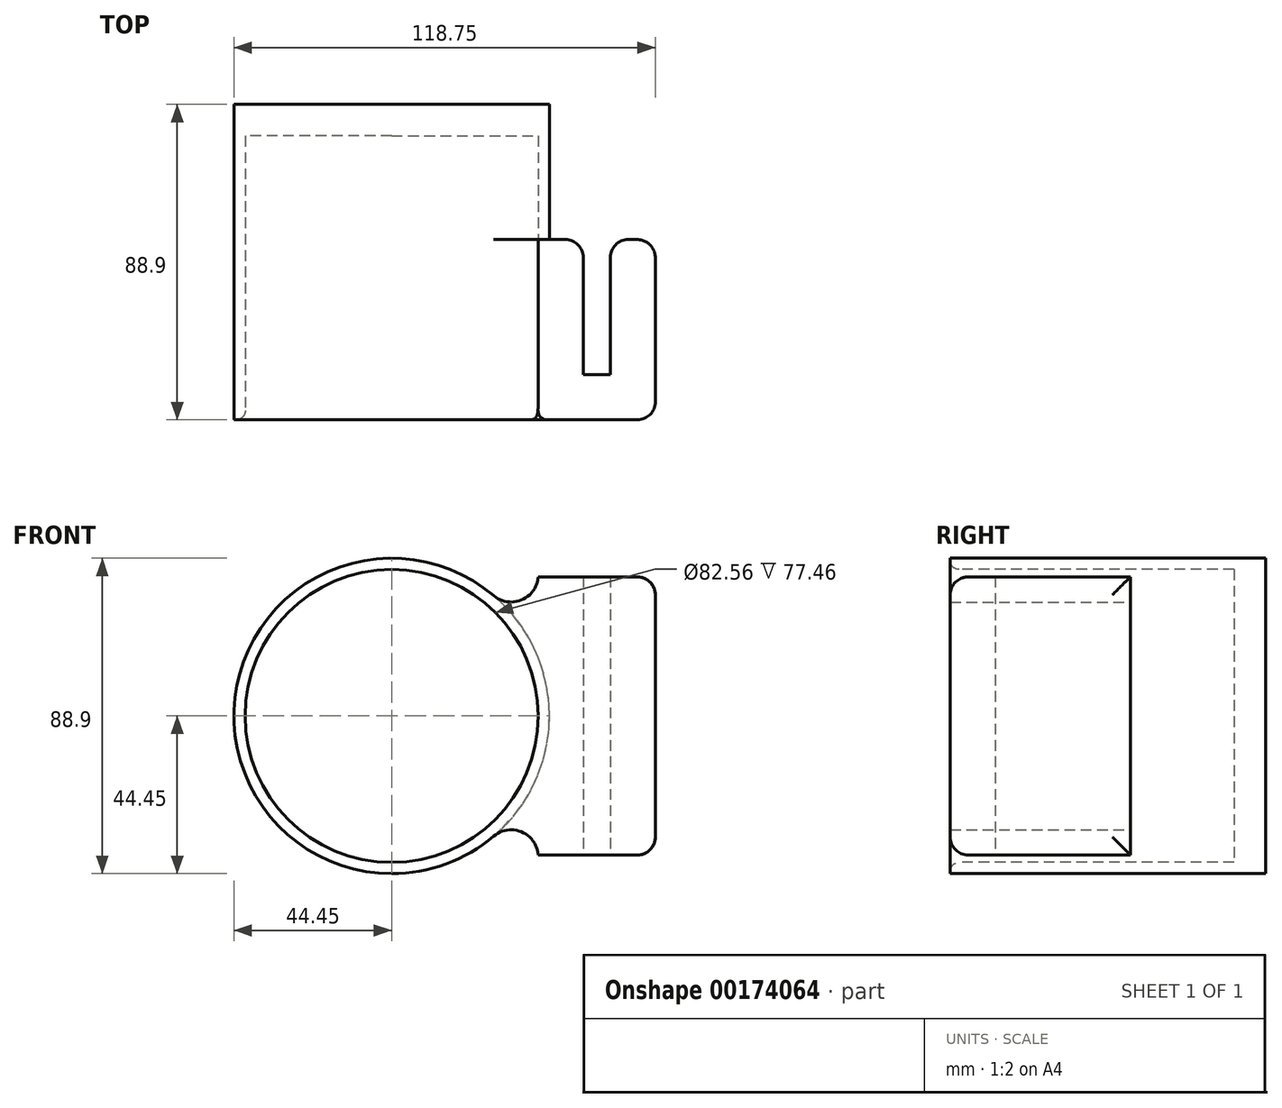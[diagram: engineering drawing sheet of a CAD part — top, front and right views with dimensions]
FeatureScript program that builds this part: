
annotation { "Feature Type Name" : "Feature", "Feature Type Description" : "" }
export const myFeature = defineFeature(function(context is Context, id is Id, definition is map)
    precondition{}
    {
        {
            var Q0;
            Q0=qCreatedBy(makeId("Front.planeOp"),FACE);
            var sketch = newSketch(context, id + "F0", { "sketchPlane" : qUnion([Q0])});
            skCircle(sketch, "E0", {"center": v(0, 0) * mm, "radius": 44.45 * mm});
            skCircle(sketch, "E1", {"center": v(0, 0) * mm, "radius": 41.28 * mm});
            skLineSegment(sketch, "E2.bottom", {"start": v(41.27, 39.2) * mm, "end": v(74.3, 39.2) * mm});
            skLineSegment(sketch, "E2.top", {"start": v(41.27, -39.2) * mm, "end": v(74.3, -39.2) * mm});
            skLineSegment(sketch, "E2.left", {"start": v(41.27, 39.2) * mm, "end": v(41.27, -39.2) * mm});
            skLineSegment(sketch, "E2.right", {"start": v(74.3, 39.2) * mm, "end": v(74.3, -39.2) * mm});
            skPoint(sketch, "E2.middle", {"position": v(57.78, 0) * mm});
            skLineSegment(sketch, "E3", {"start": v(53.97, 39.2) * mm, "end": v(53.97, -39.2) * mm});
            skLineSegment(sketch, "E4", {"start": v(61.6, 39.2) * mm, "end": v(61.6, -39.2) * mm});
            skCircle(sketch, "E5", {"center": v(0, 0) * mm, "radius": 11.37 * mm});
            skSolve(sketch);
        }
        {
            var Q0;
            {var subQ7=sQuery(id+"F0.wireOp",EDGE,"E3");Q0=makeQuery(id+"F0.imprint","IMPRINT",FACE,{"disambiguationData":[TD([[makeQuery(id+"F0.imprint","IMPRINT",EDGE,{"derivedFrom":subQ7}),-1.0]])]});}
            var Q1;
            {var subQ0=sQuery(id+"F0.wireOp",EDGE,"E2.right");Q1=makeQuery(id+"F0.imprint","IMPRINT",FACE,{"disambiguationData":[TD([[makeQuery(id+"F0.imprint","IMPRINT",EDGE,{"derivedFrom":subQ0}),-1.0]])]});}
            extrude(context, id + "F1", {"entities" : qUnion([Q0, Q1]), "oppositeDirection" : true, "depth" : 50.8 * mm});
        }
        {
            var Q0;
            {var subQ0=sQuery(id+"F0.wireOp",EDGE,"E3");Q0=makeQuery(id+"F0.imprint","IMPRINT",FACE,{"disambiguationData":[TD([[makeQuery(id+"F0.imprint","IMPRINT",EDGE,{"derivedFrom":subQ0}),1.0]])]});}
            extrude(context, id + "F2", {"entities" : qUnion([Q0]), "oppositeDirection" : true, "depth" : 12.7 * mm});
        }
        {
            var Q0;
            {var subQ0=sQuery(id+"F0.wireOp",EDGE,"E2.left");var subQ1=sQuery(id+"F0.wireOp",EDGE,"E0");var subQ2=makeQuery(id+"F0.imprint","INTERSECT",VERTEX,{"disambiguationData":[OD(0.0)],"derivedFrom":[subQ1,subQ0]});Q0=makeQuery(id+"F0.imprint","IMPRINT",FACE,{"disambiguationData":[TD([[makeQuery(id+"F0.imprint","IMPRINT",EDGE,{"disambiguationData":[TD([[subQ2,-1.0]])],"derivedFrom":subQ1}),1.0]])]});}
            extrude(context, id + "F3", {"entities" : qUnion([Q0]), "oppositeDirection" : true, "depth" : 88.9 * mm});
        }
        {
            var Q0;
            Q0=makeQuery(id+"F2.opExtrude","SWEPT_BODY",BODY,{"disambiguationData":[OSD([sQuery(id+"F0.wireOp",EDGE,"E2.bottom"),sQuery(id+"F0.wireOp",EDGE,"E2.top"),sQuery(id+"F0.wireOp",EDGE,"E3"),sQuery(id+"F0.wireOp",EDGE,"E4")])]});
            var Q1;
            Q1=makeQuery(id+"F3.opExtrude","SWEPT_BODY",BODY,{"disambiguationData":[OSD([sQuery(id+"F0.wireOp",EDGE,"E0"),sQuery(id+"F0.wireOp",EDGE,"E1"),sQuery(id+"F0.wireOp",EDGE,"E2.left")])]});
            var Q2;
            Q2=makeQuery(id+"F1.opExtrude","SWEPT_BODY",BODY,{"disambiguationData":[OSD([sQuery(id+"F0.wireOp",EDGE,"E2.bottom"),sQuery(id+"F0.wireOp",EDGE,"E2.top"),sQuery(id+"F0.wireOp",EDGE,"E2.right"),sQuery(id+"F0.wireOp",EDGE,"E4")])]});
            var Q3;
            Q3=makeQuery(id+"F1.opExtrude","SWEPT_BODY",BODY,{"disambiguationData":[OSD([sQuery(id+"F0.wireOp",EDGE,"E0"),sQuery(id+"F0.wireOp",EDGE,"E2.bottom"),sQuery(id+"F0.wireOp",EDGE,"E2.top"),sQuery(id+"F0.wireOp",EDGE,"E2.left"),sQuery(id+"F0.wireOp",EDGE,"E3")])]});
            booleanBodies(context, id + "F4", {"operationType" : BooleanOperationType.UNION, "tools" : qUnion([Q0, Q1, Q2, Q3])});
        }
        {
            var Q0;
            {var subQ0=sQuery(id+"F0.wireOp",EDGE,"E2.left");var subQ1=sQuery(id+"F0.wireOp",EDGE,"E0");var subQ2=makeQuery(id+"F0.imprint","INTERSECT",VERTEX,{"disambiguationData":[OD(0.0)],"derivedFrom":[subQ1,subQ0]});Q0=makeQuery(id+"F0.imprint","IMPRINT",FACE,{"disambiguationData":[TD([[makeQuery(id+"F0.imprint","IMPRINT",EDGE,{"disambiguationData":[TD([[subQ2,1.0]])],"derivedFrom":subQ1}),1.0]])]});}
            extrude(context, id + "F5", {"entities" : qUnion([Q0]), "oppositeDirection" : true, "depth" : 88.9 * mm});
        }
        {
            var Q0;
            Q0=makeQuery(id+"F2.opExtrude","SWEPT_BODY",BODY,{"disambiguationData":[OSD([sQuery(id+"F0.wireOp",EDGE,"E2.bottom"),sQuery(id+"F0.wireOp",EDGE,"E2.top"),sQuery(id+"F0.wireOp",EDGE,"E3"),sQuery(id+"F0.wireOp",EDGE,"E4")])]});
            var Q1;
            Q1=makeQuery(id+"F3.opExtrude","SWEPT_BODY",BODY,{"disambiguationData":[OSD([sQuery(id+"F0.wireOp",EDGE,"E0"),sQuery(id+"F0.wireOp",EDGE,"E1"),sQuery(id+"F0.wireOp",EDGE,"E2.left")])]});
            var Q2;
            Q2=makeQuery(id+"F5.opExtrude","SWEPT_BODY",BODY,{"disambiguationData":[OSD([sQuery(id+"F0.wireOp",EDGE,"E0"),sQuery(id+"F0.wireOp",EDGE,"E1"),sQuery(id+"F0.wireOp",EDGE,"E2.left")])]});
            booleanBodies(context, id + "F6", {"operationType" : BooleanOperationType.UNION, "tools" : qUnion([Q0, Q1, Q2])});
        }
        {
            var Q0;
            {var subQ0=sQuery(id+"F0.wireOp",EDGE,"E2.left");var subQ1=sQuery(id+"F0.wireOp",EDGE,"E0");Q0=makeQuery(id+"F1.opExtrude","SWEPT_EDGE",EDGE,{"disambiguationData":[OSD([subQ1,subQ0]),TDD([makeQuery(id+"F0.imprint","INTERSECT",VERTEX,{"disambiguationData":[OD(1.0)],"derivedFrom":[subQ1,subQ0]})])]});}
            var Q1;
            {var subQ0=sQuery(id+"F0.wireOp",EDGE,"E2.left");var subQ1=sQuery(id+"F0.wireOp",EDGE,"E0");Q1=makeQuery(id+"F1.opExtrude","SWEPT_EDGE",EDGE,{"disambiguationData":[OSD([subQ1,subQ0]),TDD([makeQuery(id+"F0.imprint","INTERSECT",VERTEX,{"disambiguationData":[OD(0.0)],"derivedFrom":[subQ1,subQ0]})])]});}
            fillet(context, id + "F7", {"entities" : qUnion([Q0, Q1]), "radius" : 7.62 * mm, "tangentPropagation" : true, "allowEdgeOverflow" : false});
        }
        {
            var Q0;
            Q0=makeQuery(id+"F1.opExtrude","CAP_EDGE",EDGE,{"disambiguationData":[OSD([sQuery(id+"F0.wireOp",EDGE,"E3")])],"isStart":false});
            var Q1;
            Q1=makeQuery(id+"F1.opExtrude","CAP_EDGE",EDGE,{"disambiguationData":[OSD([sQuery(id+"F0.wireOp",EDGE,"E4")])],"isStart":false});
            var Q2;
            Q2=makeQuery(id+"F1.opExtrude","CAP_EDGE",EDGE,{"disambiguationData":[OSD([sQuery(id+"F0.wireOp",EDGE,"E2.right")])],"isStart":true});
            var Q3;
            {var subQ0=sQuery(id+"F0.wireOp",EDGE,"E2.top");Q3=makeQuery(id+"F4.opBoolean","MERGE",EDGE,{"derivedFrom":[makeQuery(id+"F1.opExtrude","CAP_EDGE",EDGE,{"disambiguationData":[OSD([subQ0]),TDD([makeQuery(id+"F0.imprint","IMPRINT",EDGE,{"disambiguationData":[TD([[makeQuery(id+"F0.imprint","INTERSECT",VERTEX,{"derivedFrom":[subQ0,sQuery(id+"F0.wireOp",EDGE,"E2.left")]}),-1.0]])],"derivedFrom":subQ0})])],"isStart":true}),makeQuery(id+"F1.opExtrude","CAP_EDGE",EDGE,{"disambiguationData":[OSD([subQ0]),TDD([makeQuery(id+"F0.imprint","IMPRINT",EDGE,{"disambiguationData":[TD([[makeQuery(id+"F0.imprint","INTERSECT",VERTEX,{"derivedFrom":[subQ0,sQuery(id+"F0.wireOp",EDGE,"E2.right")]}),1.0]])],"derivedFrom":subQ0})])],"isStart":true}),makeQuery(id+"F2.opExtrude","CAP_EDGE",EDGE,{"disambiguationData":[OSD([subQ0])],"isStart":true})]});}
            var Q4;
            {var subQ0=sQuery(id+"F0.wireOp",EDGE,"E2.bottom");Q4=makeQuery(id+"F4.opBoolean","MERGE",EDGE,{"derivedFrom":[makeQuery(id+"F1.opExtrude","CAP_EDGE",EDGE,{"disambiguationData":[OSD([subQ0]),TDD([makeQuery(id+"F0.imprint","IMPRINT",EDGE,{"disambiguationData":[TD([[makeQuery(id+"F0.imprint","INTERSECT",VERTEX,{"derivedFrom":[subQ0,sQuery(id+"F0.wireOp",EDGE,"E2.left")]}),-1.0]])],"derivedFrom":subQ0})])],"isStart":true}),makeQuery(id+"F1.opExtrude","CAP_EDGE",EDGE,{"disambiguationData":[OSD([subQ0]),TDD([makeQuery(id+"F0.imprint","IMPRINT",EDGE,{"disambiguationData":[TD([[makeQuery(id+"F0.imprint","INTERSECT",VERTEX,{"derivedFrom":[subQ0,sQuery(id+"F0.wireOp",EDGE,"E2.right")]}),1.0]])],"derivedFrom":subQ0})])],"isStart":true}),makeQuery(id+"F2.opExtrude","CAP_EDGE",EDGE,{"disambiguationData":[OSD([subQ0])],"isStart":true})]});}
            var Q5;
            Q5=makeQuery(id+"F1.opExtrude","CAP_EDGE",EDGE,{"disambiguationData":[OSD([sQuery(id+"F0.wireOp",EDGE,"E2.right")])],"isStart":false});
            var Q6;
            Q6=makeQuery(id+"F1.opExtrude","SWEPT_EDGE",EDGE,{"disambiguationData":[OSD([sQuery(id+"F0.wireOp",EDGE,"E2.top"),sQuery(id+"F0.wireOp",EDGE,"E2.right")])]});
            var Q7;
            Q7=makeQuery(id+"F1.opExtrude","SWEPT_EDGE",EDGE,{"disambiguationData":[OSD([sQuery(id+"F0.wireOp",EDGE,"E2.bottom"),sQuery(id+"F0.wireOp",EDGE,"E2.right")])]});
            fillet(context, id + "F8", {"entities" : qUnion([Q0, Q1, Q2, Q3, Q4, Q5, Q6, Q7]), "radius" : 5.08 * mm, "tangentPropagation" : true, "allowEdgeOverflow" : false});
        }
        {
            var Q0;
            {var subQ0=sQuery(id+"F0.wireOp",EDGE,"E1");Q0=makeQuery(id+"F6.opBoolean","MERGE",EDGE,{"derivedFrom":[makeQuery(id+"F3.opExtrude","CAP_EDGE",EDGE,{"disambiguationData":[OSD([subQ0])],"isStart":true}),makeQuery(id+"F5.opExtrude","CAP_EDGE",EDGE,{"disambiguationData":[OSD([subQ0])],"isStart":true})]});}
            fillet(context, id + "F9", {"entities" : qUnion([Q0]), "radius" : 2.54 * mm, "tangentPropagation" : true, "allowEdgeOverflow" : false});
        }
        {
            var Q0;
            {var subQ0=sQuery(id+"F0.wireOp",EDGE,"E2.left");var subQ1=sQuery(id+"F0.wireOp",EDGE,"E1");var subQ2=sQuery(id+"F0.wireOp",EDGE,"E0");Q0=makeQuery(id+"F6.opBoolean","MERGE",FACE,{"derivedFrom":[makeQuery(id+"F3.opExtrude","CAP_FACE",FACE,{"disambiguationData":[OSD([subQ2,subQ1,subQ0])],"isStart":false}),makeQuery(id+"F5.opExtrude","CAP_FACE",FACE,{"disambiguationData":[OSD([subQ2,subQ1,subQ0])],"isStart":false})]});}
            cPlane(context, id + "F10", {"entities" : qUnion([Q0]), "cplaneType" : CPlaneType.OFFSET, "offset" : 0 * mm, "width" : 152.4 * mm, "height" : 152.4 * mm});
        }
        {
            var Q0;
            Q0=qCreatedBy(id+"F10.planeOp",FACE);
            var sketch = newSketch(context, id + "F11", { "sketchPlane" : qUnion([Q0])});
            skCircle(sketch, "E6", {"center": v(0, 0) * mm, "radius": 44.45 * mm});
            skSolve(sketch);
        }
        {
            var Q0;
            Q0=makeQuery(id+"F11.imprint","IMPRINT",FACE,{"disambiguationData":[TD([[makeQuery(id+"F11.imprint","IMPRINT",EDGE,{"derivedFrom":sQuery(id+"F11.wireOp",EDGE,"E6")}),1.0]])]});
            extrude(context, id + "F12", {"entities" : qUnion([Q0]), "operationType" : NewBodyOperationType.ADD, "oppositeDirection" : true, "depth" : 8.9 * mm});
        }
    });
